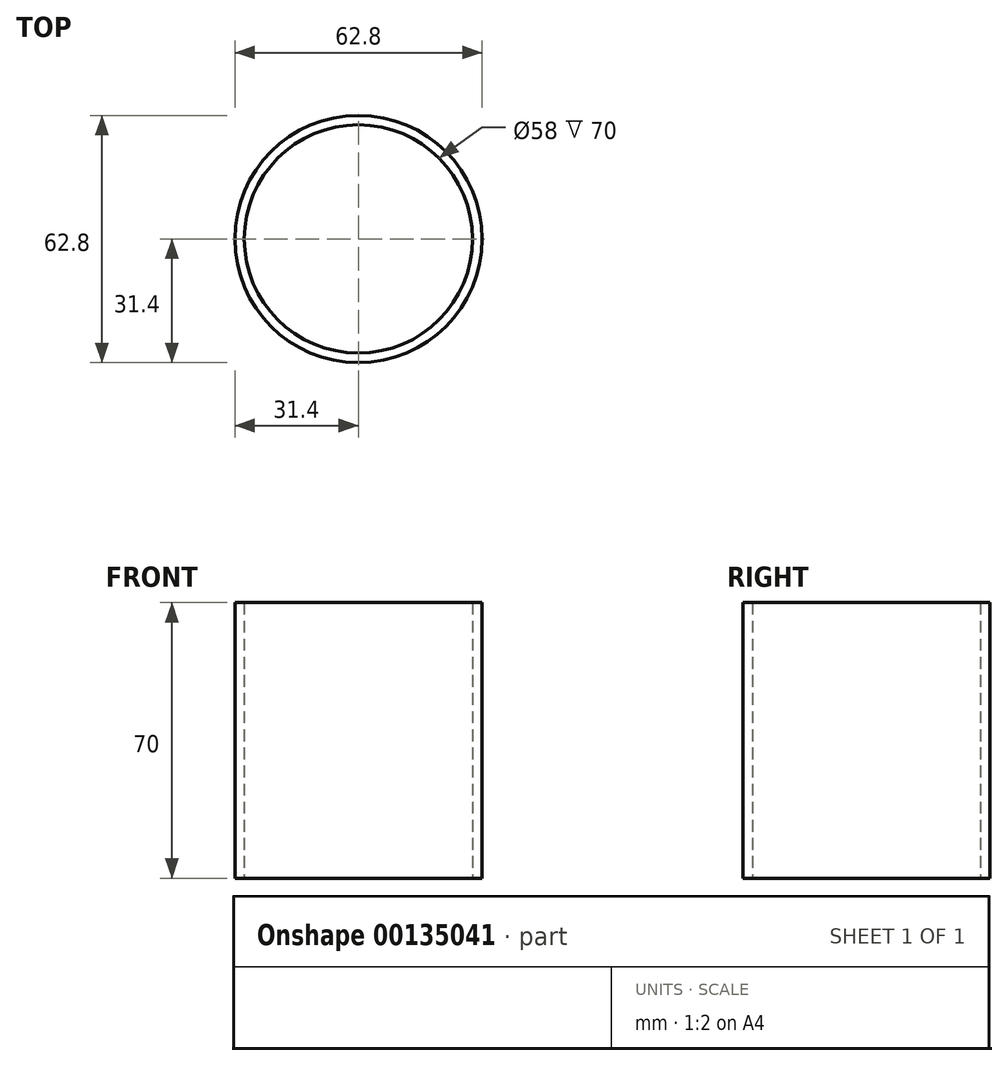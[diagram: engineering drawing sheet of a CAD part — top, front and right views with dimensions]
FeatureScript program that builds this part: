
annotation { "Feature Type Name" : "Feature", "Feature Type Description" : "" }
export const myFeature = defineFeature(function(context is Context, id is Id, definition is map)
    precondition{}
    {
        {
            var Q0;
            Q0=qCreatedBy(makeId("Top.planeOp"),FACE);
            var sketch = newSketch(context, id + "F0", { "sketchPlane" : qUnion([Q0])});
            skCircle(sketch, "E0", {"center": v(0, 0) * mm, "radius": 29 * mm});
            skCircle(sketch, "E1", {"center": v(0, 0) * mm, "radius": 31.4 * mm});
            skSolve(sketch);
        }
        {
            var Q0;
            Q0=makeQuery(id+"F0.imprint","IMPRINT",FACE,{"disambiguationData":[TD([[makeQuery(id+"F0.imprint","IMPRINT",EDGE,{"derivedFrom":sQuery(id+"F0.wireOp",EDGE,"E0")}),-1.0]])]});
            extrude(context, id + "F1", {"entities" : qUnion([Q0]), "depth" : 70 * mm});
        }
    });
